# Revit family: Key Management Systems_Traka Touch_Traka ASSA ABLOY_S-Touch Key Cabinet_
name_source: partatom
category: Generic Models
revit_build: Autodesk Revit 2015 (Build: 20140903_1530(x64)
units: mm (PartAtom-declared; Revit-internal decimal feet)

## types (1)
- S-Touch Key Cabinet_KEYSYS-TTS-60
    Article Number = KEYSYS-TTS-60
    BIMobject  Product family = Key management systems
    BIMobject Brand = Traka ASSA ABLOY
    BIMobject Instructions Video = https://youtu.be
    BIMobject Product Page = https://bimobject.com
    BIMobject Product group = S-series touch
    BIMobject Unique ref = s-series-touch
    BIMobject category = Security, Cameras & Accessories
    Date of publishing = 8/12/2016
    Depth = 140 mm
    Description = S Series Touch system 60 iFob Locking complete
    Door Material = Traka_Clear Polycarbonate
    Edition number = 1
    Finish = Traka_Black fine texture (TLP-F652-T)
    Height = 675 mm
    IFC Classification = Furnishing Element
    ISO = ISO 14001, ISO 9001
    Instructions Video = https://youtu.be
    Manufacturer = Traka ASSA ABLOY
    Material main = Steel
    Material secondary = Polycarbonate
    Model = Key Management Systems_Traka Touch_Traka ASSA ABLOY_S-Touch Key Cabinet
    NBS Reference Code = 75-40-02
    NBS Reference Description = Access Control Systems
    Name = S-Touch Key Cabinet
    Nominal Voltage = 240 V
    OmniClass Code = 23-21 35 21 23
    OmniClass Description = Key Security Cabinets
    Product Datasheet = http://www.traka.com
    Product Group = Key Management Systems
    Product Guid = 5d60c50f-9426-426a-a9a9-db34965ad7bd
    Product Range = Traka Touch
    Provider = Traka ASSA ABLOY
    Reference Standards = CE, FCC, CSA, ROHS
    Type Comments = S-Touch Key Cabinet_KEYSYS-TTS-60
    UNSPSC Code = 46171509
    URL = http://www.traka.com
    Uniclass 1.4 Code = JW40
    Uniclass 1.4 Description = Access control systems
    Uniclass 2.0 Code = SS-75-40-02
    Uniclass 2.0 Description = Access Control Systems
    Uniclass 2015 Code = Pr_80_77_28_60
    Uniclass 2015 Name = Padlock and key cabinets
    Weight = 29 kg
    Width = 866 mm

## geometry (parser evidence)
native form markers: Sweep x6
no freeform markers — native parametric forms only
